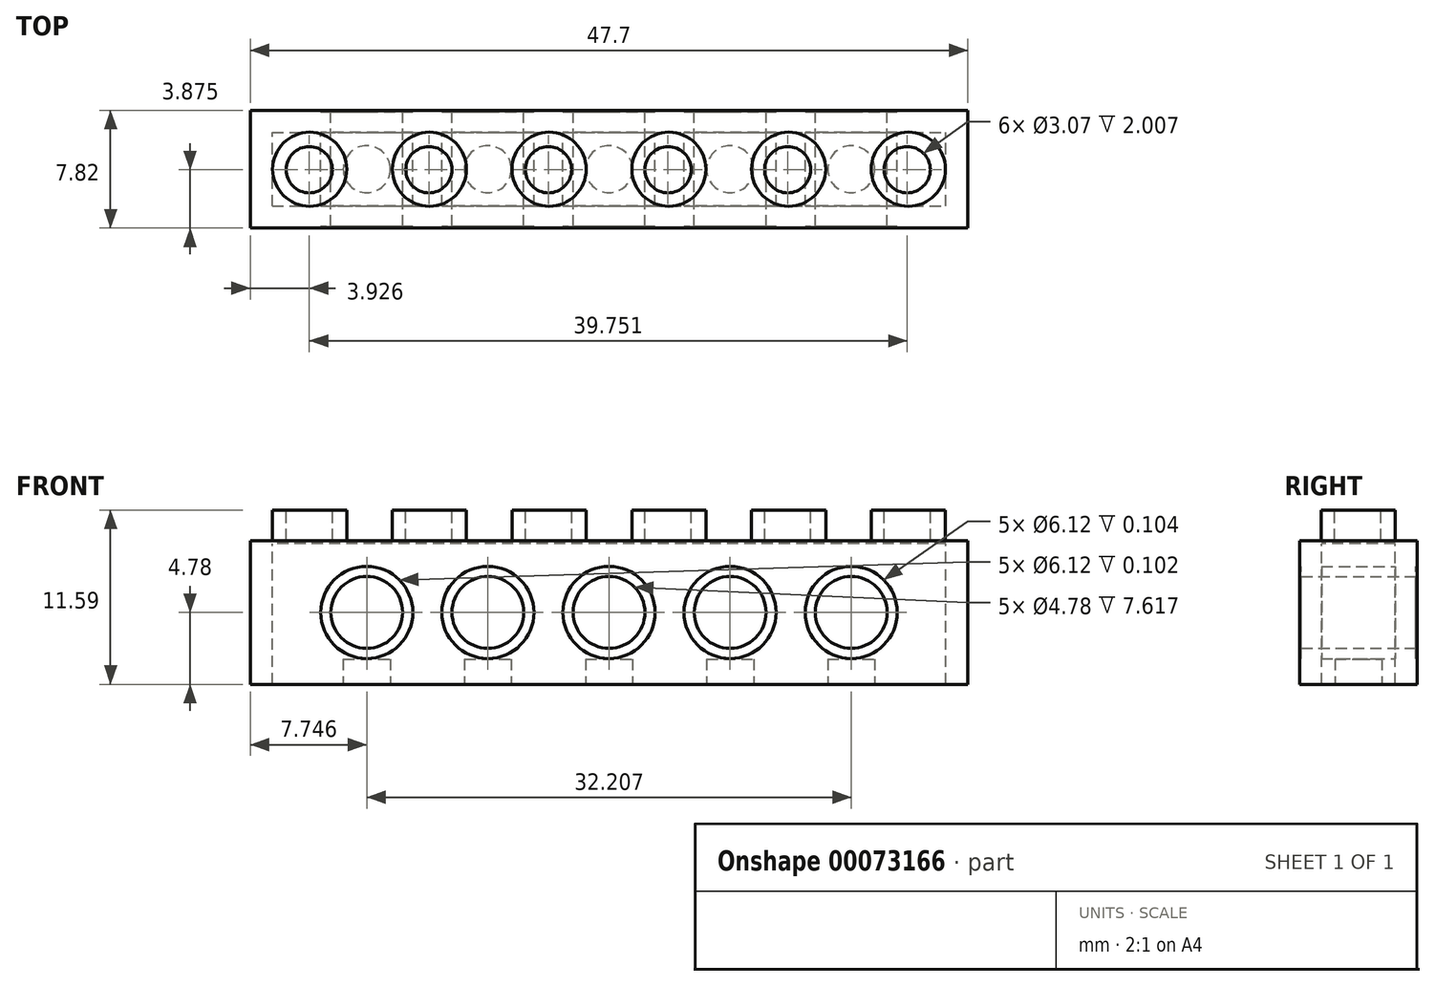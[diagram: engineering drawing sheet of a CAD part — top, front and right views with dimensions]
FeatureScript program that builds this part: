
annotation { "Feature Type Name" : "Feature", "Feature Type Description" : "" }
export const myFeature = defineFeature(function(context is Context, id is Id, definition is map)
    precondition{}
    {
        {
            var Q0;
            Q0=qCreatedBy(makeId("Front.planeOp"),FACE);
            var sketch = newSketch(context, id + "F0", { "sketchPlane" : qUnion([Q0])});
            skLineSegment(sketch, "E0.bottom", {"start": v(23.85, -4.78) * mm, "end": v(-23.85, -4.78) * mm});
            skLineSegment(sketch, "E0.top", {"start": v(23.85, 4.78) * mm, "end": v(-23.85, 4.78) * mm});
            skLineSegment(sketch, "E0.left", {"start": v(23.85, -4.78) * mm, "end": v(23.85, 4.78) * mm});
            skLineSegment(sketch, "E0.right", {"start": v(-23.85, -4.78) * mm, "end": v(-23.85, 4.78) * mm});
            skPoint(sketch, "E0.middle", {"position": v(0, 0) * mm});
            skSolve(sketch);
        }
        {
            var Q0;
            Q0 = qSketchRegion(id + "F0", true);
            extrude(context, id + "F1", {"entities" : qUnion([Q0]), "depth" : 7.82 * mm});
        }
        {
            var Q0;
            Q0=qCreatedBy(makeId("Top.planeOp"),FACE);
            var sketch = newSketch(context, id + "F2", { "sketchPlane" : qUnion([Q0])});
            skLineSegment(sketch, "E1", {"start": v(0, -7.82) * mm, "end": v(0, 0) * mm});
            skLineSegment(sketch, "E2.bottom", {"start": v(22.4, -1.46) * mm, "end": v(-22.4, -1.46) * mm});
            skLineSegment(sketch, "E2.top", {"start": v(22.4, -6.36) * mm, "end": v(-22.4, -6.36) * mm});
            skLineSegment(sketch, "E2.left", {"start": v(22.4, -1.46) * mm, "end": v(22.4, -6.36) * mm});
            skLineSegment(sketch, "E2.right", {"start": v(-22.4, -1.46) * mm, "end": v(-22.4, -6.36) * mm});
            skPoint(sketch, "E2.middle", {"position": v(0, -3.91) * mm});
            skSolve(sketch);
        }
        {
            var Q0;
            Q0 = qSketchRegion(id + "F2", true);
            extrude(context, id + "F3", {"entities" : qUnion([Q0]), "operationType" : NewBodyOperationType.REMOVE, "endBound" : BoundingType.THROUGH_ALL, "oppositeDirection" : true, "depth" : 5.34 * mm, "hasSecondDirection" : true, "secondDirectionOppositeDirection" : false, "secondDirectionDepth" : 4.57 * mm});
        }
        {
            var Q0;
            Q0=qCreatedBy(makeId("Top.planeOp"),FACE);
            var sketch = newSketch(context, id + "F4", { "sketchPlane" : qUnion([Q0])});
            skLineSegment(sketch, "E3", {"start": v(-19.9, 0) * mm, "end": v(-19.9, -7.82) * mm, "construction": true});
            skCircle(sketch, "E4", {"center": v(-19.9, -3.91) * mm, "radius": 2.46 * mm});
            skLineSegment(sketch, "E5", {"start": v(-23.85, 0) * mm, "end": v(-23.85, -7.82) * mm});
            skLineSegment(sketch, "E6", {"start": v(-23.85, 0) * mm, "end": v(0, 0) * mm});
            skCircle(sketch, "E7.1.0.0", {"center": v(-11.94, -3.91) * mm, "radius": 2.46 * mm});
            skCircle(sketch, "E7.2.0.0", {"center": v(-3.98, -3.91) * mm, "radius": 2.46 * mm});
            skCircle(sketch, "E7.3.0.0", {"center": v(3.98, -3.91) * mm, "radius": 2.46 * mm});
            skCircle(sketch, "E7.4.0.0", {"center": v(11.94, -3.91) * mm, "radius": 2.46 * mm});
            skCircle(sketch, "E7.5.0.0", {"center": v(19.9, -3.91) * mm, "radius": 2.46 * mm});
            skLineSegment(sketch, "E7.direction1", {"start": v(-19.9, -3.91) * mm, "end": v(-11.94, -3.91) * mm, "construction": true});
            skSolve(sketch);
        }
        {
            var Q0;
            Q0=makeQuery(id+"F4.imprint","IMPRINT",FACE,{"disambiguationData":[TD([[makeQuery(id+"F4.imprint","IMPRINT",EDGE,{"derivedFrom":sQuery(id+"F4.wireOp",EDGE,"E4")}),1.0]])]});
            var Q1;
            Q1=makeQuery(id+"F4.imprint","IMPRINT",FACE,{"disambiguationData":[TD([[makeQuery(id+"F4.imprint","IMPRINT",EDGE,{"derivedFrom":sQuery(id+"F4.wireOp",EDGE,"E7.1.0.0")}),1.0]])]});
            var Q2;
            Q2=makeQuery(id+"F4.imprint","IMPRINT",FACE,{"disambiguationData":[TD([[makeQuery(id+"F4.imprint","IMPRINT",EDGE,{"derivedFrom":sQuery(id+"F4.wireOp",EDGE,"E7.2.0.0")}),1.0]])]});
            var Q3;
            Q3=makeQuery(id+"F4.imprint","IMPRINT",FACE,{"disambiguationData":[TD([[makeQuery(id+"F4.imprint","IMPRINT",EDGE,{"derivedFrom":sQuery(id+"F4.wireOp",EDGE,"E7.3.0.0")}),1.0]])]});
            var Q4;
            Q4=makeQuery(id+"F4.imprint","IMPRINT",FACE,{"disambiguationData":[TD([[makeQuery(id+"F4.imprint","IMPRINT",EDGE,{"derivedFrom":sQuery(id+"F4.wireOp",EDGE,"E7.4.0.0")}),1.0]])]});
            var Q5;
            Q5=makeQuery(id+"F4.imprint","IMPRINT",FACE,{"disambiguationData":[TD([[makeQuery(id+"F4.imprint","IMPRINT",EDGE,{"derivedFrom":sQuery(id+"F4.wireOp",EDGE,"E7.5.0.0")}),1.0]])]});
            extrude(context, id + "F5", {"entities" : qUnion([Q0, Q1, Q2, Q3, Q4, Q5]), "operationType" : NewBodyOperationType.ADD, "depth" : 6.8 * mm, "hasSecondDirection" : true, "secondDirectionOppositeDirection" : false, "secondDirectionDepth" : 4.66 * mm});
        }
        {
            var Q0;
            Q0=makeQuery(id+"F5.opExtrude","CAP_FACE",FACE,{"disambiguationData":[OSD([sQuery(id+"F4.wireOp",EDGE,"E4")])],"isStart":false});
            cPlane(context, id + "F6", {"entities" : qUnion([Q0]), "cplaneType" : CPlaneType.OFFSET, "offset" : 152.4 * mm, "width" : 152.4 * mm, "height" : 152.4 * mm});
        }
        {
            var Q0;
            Q0=qCreatedBy(id+"F6.planeOp",FACE);
            var sketch = newSketch(context, id + "F7", { "sketchPlane" : qUnion([Q0])});
            skCircle(sketch, "E8", {"center": v(19.83, -3.94) * mm, "radius": 1.54 * mm});
            skCircle(sketch, "E9.1.0.0", {"center": v(11.88, -3.94) * mm, "radius": 1.54 * mm});
            skCircle(sketch, "E9.2.0.0", {"center": v(3.93, -3.94) * mm, "radius": 1.54 * mm});
            skCircle(sketch, "E9.3.0.0", {"center": v(-4.02, -3.94) * mm, "radius": 1.54 * mm});
            skCircle(sketch, "E9.4.0.0", {"center": v(-11.97, -3.94) * mm, "radius": 1.54 * mm});
            skCircle(sketch, "E9.5.0.0", {"center": v(-19.92, -3.94) * mm, "radius": 1.54 * mm});
            skLineSegment(sketch, "E9.direction1", {"start": v(19.83, -3.94) * mm, "end": v(11.88, -3.94) * mm, "construction": true});
            skSolve(sketch);
        }
        {
            var Q0;
            Q0 = qSketchRegion(id + "F7", true);
            extrude(context, id + "F8", {"entities" : qUnion([Q0]), "operationType" : NewBodyOperationType.REMOVE, "oppositeDirection" : true, "depth" : 154.4 * mm});
        }
        {
            var Q0;
            Q0=qCreatedBy(makeId("Front.planeOp"),FACE);
            var sketch = newSketch(context, id + "F9", { "sketchPlane" : qUnion([Q0])});
            skCircle(sketch, "E10", {"center": v(0, 0) * mm, "radius": 3.06 * mm});
            skCircle(sketch, "E11.1.0.0", {"center": v(8.05, 0) * mm, "radius": 3.06 * mm});
            skCircle(sketch, "E11.2.0.0", {"center": v(16.1, 0) * mm, "radius": 3.06 * mm});
            skLineSegment(sketch, "E11.direction1", {"start": v(0, 0) * mm, "end": v(8.05, 0) * mm, "construction": true});
            skCircle(sketch, "E12.2.0.0", {"center": v(-8.05, 0) * mm, "radius": 3.06 * mm});
            skCircle(sketch, "E12.3.0.0", {"center": v(-16.1, 0) * mm, "radius": 3.06 * mm});
            skLineSegment(sketch, "E12.direction1", {"start": v(8.05, 0) * mm, "end": v(0, 0) * mm, "construction": true});
            skSolve(sketch);
        }
        {
            var Q0;
            Q0 = qSketchRegion(id + "F9", true);
            extrude(context, id + "F10", {"entities" : qUnion([Q0]), "operationType" : NewBodyOperationType.REMOVE, "depth" : 9.14 * mm});
        }
        {
            var Q0;
            Q0=qCreatedBy(makeId("Front.planeOp"),FACE);
            var sketch = newSketch(context, id + "F11", { "sketchPlane" : qUnion([Q0])});
            skCircle(sketch, "E13", {"center": v(0, 0) * mm, "radius": 2.39 * mm});
            skCircle(sketch, "E14", {"center": v(0, 0) * mm, "radius": 3.06 * mm});
            skCircle(sketch, "E15.1.0.0", {"center": v(8.05, 0) * mm, "radius": 2.39 * mm});
            skCircle(sketch, "E15.1.0.1", {"center": v(8.05, 0) * mm, "radius": 3.06 * mm});
            skCircle(sketch, "E15.2.0.0", {"center": v(16.1, 0) * mm, "radius": 2.39 * mm});
            skCircle(sketch, "E15.2.0.1", {"center": v(16.1, 0) * mm, "radius": 3.06 * mm});
            skLineSegment(sketch, "E15.direction1", {"start": v(0, 0) * mm, "end": v(8.05, 0) * mm, "construction": true});
            skCircle(sketch, "E16.2.0.0", {"center": v(-8.05, 0) * mm, "radius": 2.39 * mm});
            skCircle(sketch, "E16.2.0.1", {"center": v(-8.05, 0) * mm, "radius": 3.06 * mm});
            skCircle(sketch, "E16.3.0.0", {"center": v(-16.1, 0) * mm, "radius": 2.39 * mm});
            skCircle(sketch, "E16.3.0.1", {"center": v(-16.1, 0) * mm, "radius": 3.06 * mm});
            skLineSegment(sketch, "E16.direction1", {"start": v(8.05, 0) * mm, "end": v(0, 0) * mm, "construction": true});
            skSolve(sketch);
        }
        {
            var Q0;
            Q0 = qSketchRegion(id + "F11", true);
            extrude(context, id + "F12", {"entities" : qUnion([Q0]), "operationType" : NewBodyOperationType.ADD, "depth" : 7.72 * mm, "hasSecondDirection" : true, "secondDirectionOppositeDirection" : false, "secondDirectionDepth" : 0.1 * mm});
        }
        {
            var Q0;
            Q0=makeQuery(id+"F1.opExtrude","SWEPT_FACE",FACE,{"disambiguationData":[OSD([sQuery(id+"F0.wireOp",EDGE,"E0.bottom")])]});
            cPlane(context, id + "F13", {"entities" : qUnion([Q0]), "cplaneType" : CPlaneType.OFFSET, "offset" : 0 * mm, "width" : 152.4 * mm, "height" : 152.4 * mm});
        }
        {
            var Q0;
            Q0=qCreatedBy(id+"F13.planeOp",FACE);
            var sketch = newSketch(context, id + "F14", { "sketchPlane" : qUnion([Q0])});
            skCircle(sketch, "E17", {"center": v(0, 3.91) * mm, "radius": 1.56 * mm});
            skLineSegment(sketch, "E18", {"start": v(0, 3.91) * mm, "end": v(0, 0) * mm, "construction": true});
            skCircle(sketch, "E19.1.0.0", {"center": v(8.05, 3.91) * mm, "radius": 1.56 * mm});
            skCircle(sketch, "E19.2.0.0", {"center": v(16.1, 3.91) * mm, "radius": 1.56 * mm});
            skLineSegment(sketch, "E19.direction1", {"start": v(0, 3.91) * mm, "end": v(8.05, 3.91) * mm, "construction": true});
            skCircle(sketch, "E20.2.0.0", {"center": v(-8.05, 3.91) * mm, "radius": 1.56 * mm});
            skCircle(sketch, "E20.3.0.0", {"center": v(-16.1, 3.91) * mm, "radius": 1.56 * mm});
            skLineSegment(sketch, "E20.direction1", {"start": v(8.05, 3.91) * mm, "end": v(0, 3.91) * mm, "construction": true});
            skSolve(sketch);
        }
        {
            var Q0;
            Q0 = qSketchRegion(id + "F14", true);
            extrude(context, id + "F15", {"entities" : qUnion([Q0]), "oppositeDirection" : true, "depth" : 1.68 * mm});
        }
    });
